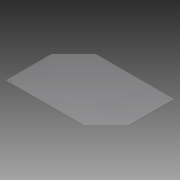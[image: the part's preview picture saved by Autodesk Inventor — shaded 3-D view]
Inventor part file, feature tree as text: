
AUTODESK INVENTOR PART (.ipt)
format: ipt  version: 2015 SP1 (Build 190203100, 203)  size: 101,888 bytes
history: native  units: in
note: dims shown in document units (in); Inventor stores cm internally (conversion verified against a paired STEP export)
features: extrude x1, sketch x1
ambient origin geometry x8: Origin, YZ Plane, XZ Plane, XY Plane, X Axis, Y Axis, Z Axis, Center Point
bodies: Body1 (feature_tree)
feature tree (2):
  extrude  "Extrusion3"  Depth=14.5in
  sketch  "Sketch1"  dims[d0=21.5in d1=14.5in d2=0.5in d3=0.5in d4=0.5in d5=0.5in d6=0.5in d7=0.5in d8=0.5in d9=0.5in d15=0.25in d16=0.25in d17=0.25in d19=0.25in d28=0.125in d29=0.0in]
